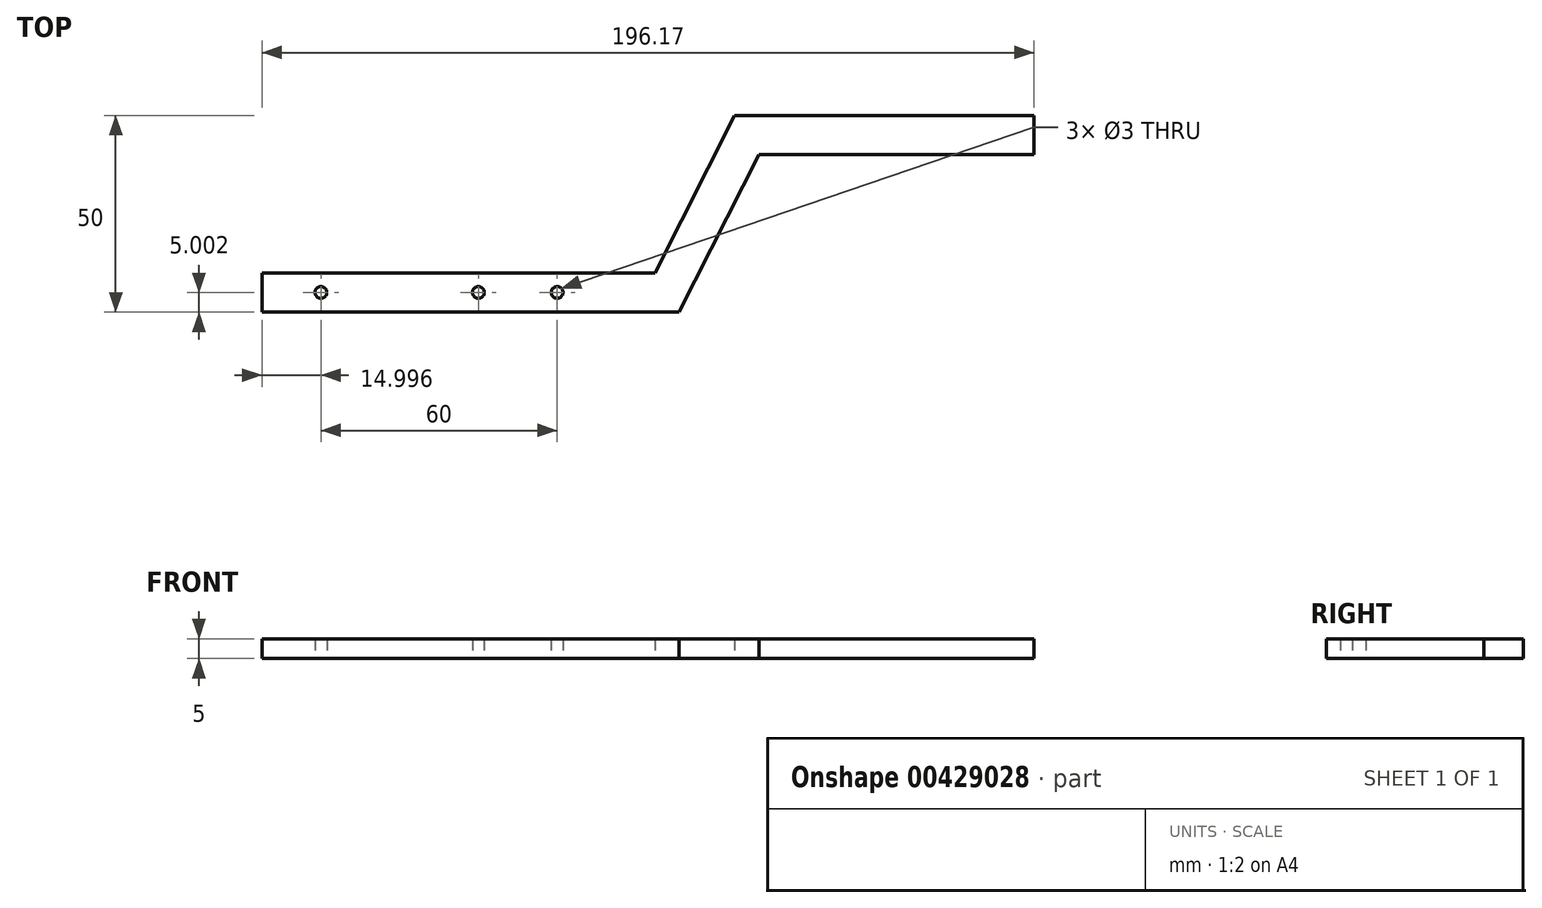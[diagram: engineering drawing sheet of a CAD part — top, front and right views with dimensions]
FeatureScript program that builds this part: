
annotation { "Feature Type Name" : "Feature", "Feature Type Description" : "" }
export const myFeature = defineFeature(function(context is Context, id is Id, definition is map)
    precondition{}
    {
        {
            var Q0;
            Q0=qCreatedBy(makeId("Top.planeOp"),FACE);
            var sketch = newSketch(context, id + "F0", { "sketchPlane" : qUnion([Q0])});
            skLineSegment(sketch, "E0", {"start": v(-151.91, -45.93) * mm, "end": v(-52.04, -45.93) * mm});
            skLineSegment(sketch, "E1.0", {"start": v(-151.91, -55.93) * mm, "end": v(-45.89, -55.93) * mm});
            skLineSegment(sketch, "E2.0", {"start": v(-31.91, -5.93) * mm, "end": v(-31.84, -5.93) * mm});
            skLineSegment(sketch, "E3", {"start": v(-31.91, -5.93) * mm, "end": v(-31.91, -6.08) * mm});
            skPoint(sketch, "E3.endSnap0", {"position": v(-31.91, -20.93) * mm});
            skLineSegment(sketch, "E4", {"start": v(-151.91, -45.93) * mm, "end": v(-151.91, -55.93) * mm});
            skPoint(sketch, "E5.orphan", {"position": v(-31.91, -83.57) * mm});
            skPoint(sketch, "E6.orphan", {"position": v(-31.91, 4.07) * mm});
            skLineSegment(sketch, "E7", {"start": v(-52.04, -45.93) * mm, "end": v(-31.84, -5.93) * mm});
            skPoint(sketch, "E8.orphan", {"position": v(-41.91, 4.07) * mm});
            skLineSegment(sketch, "E9.trimOffspring", {"start": v(-31.91, -6.08) * mm, "end": v(-31.91, -5.93) * mm});
            skPoint(sketch, "E10.orphan", {"position": v(-41.91, -45.93) * mm});
            skLineSegment(sketch, "E11", {"start": v(-25.68, -15.93) * mm, "end": v(-45.89, -55.93) * mm});
            skPoint(sketch, "E12.0.start.orphan", {"position": v(-31.91, -45.93) * mm});
            skPoint(sketch, "E13.orphan", {"position": v(-35.66, 0) * mm});
            skPoint(sketch, "E14.orphan", {"position": v(38.09, 4.07) * mm});
            skCircle(sketch, "E15", {"center": v(-76.91, -50.93) * mm, "radius": 1.5 * mm});
            skCircle(sketch, "E16", {"center": v(-96.91, -50.93) * mm, "radius": 1.5 * mm});
            skCircle(sketch, "E17", {"center": v(-136.91, -50.93) * mm, "radius": 1.5 * mm});
            skLineSegment(sketch, "E18", {"start": v(-31.91, -5.93) * mm, "end": v(27.96, -5.93) * mm});
            skLineSegment(sketch, "E19.0", {"start": v(-25.68, -15.93) * mm, "end": v(27.96, -15.93) * mm});
            skPoint(sketch, "E20.orphan", {"position": v(-40.25, -5.93) * mm});
            skLineSegment(sketch, "E21", {"start": v(44.26, -5.93) * mm, "end": v(27.96, -5.93) * mm});
            skLineSegment(sketch, "E22", {"start": v(27.96, -15.93) * mm, "end": v(44.26, -15.93) * mm});
            skLineSegment(sketch, "E23", {"start": v(44.26, -5.93) * mm, "end": v(44.26, -15.93) * mm});
            skPoint(sketch, "E24.orphan", {"position": v(44.26, 0) * mm});
            skPoint(sketch, "E25.orphan", {"position": v(52.97, -5.93) * mm});
            skSolve(sketch);
        }
        {
            var Q0;
            {var subQ1=sQuery(id+"F0.wireOp",EDGE,"E0");Q0=makeQuery(id+"F0.imprint","IMPRINT",FACE,{"disambiguationData":[TD([[makeQuery(id+"F0.imprint","IMPRINT",EDGE,{"derivedFrom":subQ1}),-1.0]])]});}
            extrude(context, id + "F1", {"entities" : qUnion([Q0]), "depth" : 5 * mm});
        }
        {
            var Q0;
            Q0=makeQuery(id+"F0.imprint","IMPRINT",FACE,{"disambiguationData":[TD([[makeQuery(id+"F0.imprint","IMPRINT",EDGE,{"derivedFrom":sQuery(id+"F0.wireOp",EDGE,"E15")}),1.0]])]});
            var Q1;
            Q1=makeQuery(id+"F0.imprint","IMPRINT",FACE,{"disambiguationData":[TD([[makeQuery(id+"F0.imprint","IMPRINT",EDGE,{"derivedFrom":sQuery(id+"F0.wireOp",EDGE,"E16")}),1.0]])]});
            extrude(context, id + "F2", {"entities" : qUnion([Q0, Q1]), "operationType" : NewBodyOperationType.REMOVE, "endBound" : BoundingType.THROUGH_ALL, "oppositeDirection" : true, "depth" : 25 * mm});
        }
    });
